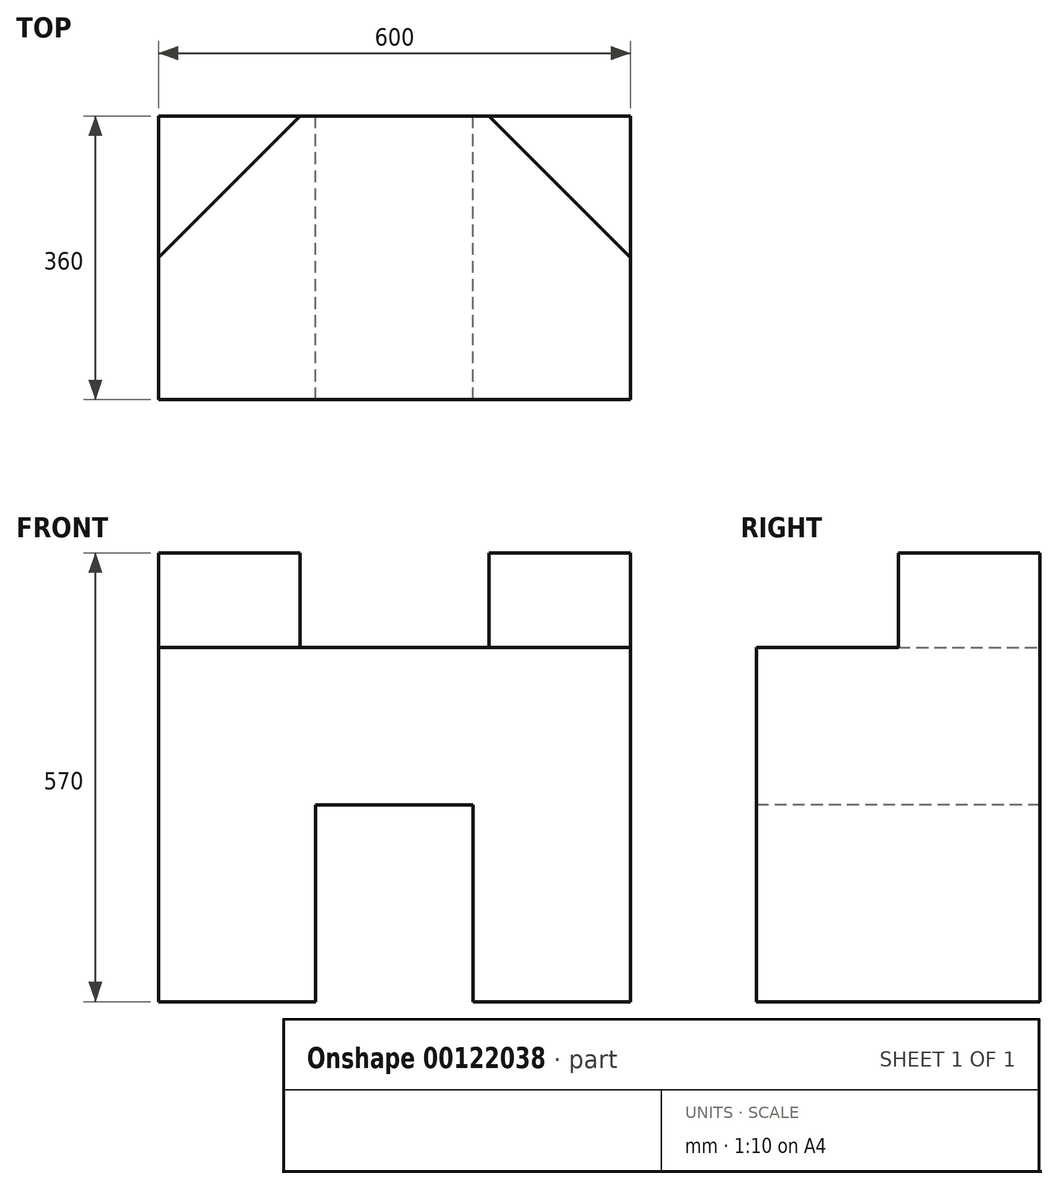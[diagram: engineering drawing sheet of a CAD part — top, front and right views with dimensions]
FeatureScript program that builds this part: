
annotation { "Feature Type Name" : "Feature", "Feature Type Description" : "" }
export const myFeature = defineFeature(function(context is Context, id is Id, definition is map)
    precondition{}
    {
        {
            var Q0;
            Q0=qCreatedBy(makeId("Front.planeOp"),FACE);
            var sketch = newSketch(context, id + "F0", { "sketchPlane" : qUnion([Q0])});
            skLineSegment(sketch, "E0.bottom", {"start": v(-300, -285) * mm, "end": v(300, -285) * mm});
            skLineSegment(sketch, "E0.top", {"start": v(-300, 285) * mm, "end": v(300, 285) * mm});
            skLineSegment(sketch, "E0.left", {"start": v(-300, -285) * mm, "end": v(-300, 285) * mm});
            skLineSegment(sketch, "E0.right", {"start": v(300, -285) * mm, "end": v(300, 285) * mm});
            skPoint(sketch, "E0.middle", {"position": v(0, 0) * mm});
            skSolve(sketch);
        }
        {
            var Q0;
            Q0 = qSketchRegion(id + "F0", true);
            extrude(context, id + "F1", {"entities" : qUnion([Q0]), "depth" : 360 * mm});
        }
        {
            var Q0;
            Q0=makeQuery(id+"F1.opExtrude","CAP_FACE",FACE,{"disambiguationData":[OSD([sQuery(id+"F0.wireOp",EDGE,"E0.bottom"),sQuery(id+"F0.wireOp",EDGE,"E0.top"),sQuery(id+"F0.wireOp",EDGE,"E0.left"),sQuery(id+"F0.wireOp",EDGE,"E0.right")])],"isStart":false});
            var sketch = newSketch(context, id + "F2", { "sketchPlane" : qUnion([Q0])});
            skLineSegment(sketch, "E1.bottom", {"start": v(-100, -535) * mm, "end": v(100, -535) * mm});
            skLineSegment(sketch, "E1.top", {"start": v(-100, -35) * mm, "end": v(100, -35) * mm});
            skLineSegment(sketch, "E1.left", {"start": v(-100, -535) * mm, "end": v(-100, -35) * mm});
            skLineSegment(sketch, "E1.right", {"start": v(100, -535) * mm, "end": v(100, -35) * mm});
            skPoint(sketch, "E1.middle", {"position": v(0, -285) * mm});
            skSolve(sketch);
        }
        {
            var Q0;
            Q0 = qSketchRegion(id + "F2", true);
            extrude(context, id + "F3", {"entities" : qUnion([Q0]), "operationType" : NewBodyOperationType.REMOVE, "endBound" : BoundingType.THROUGH_ALL, "oppositeDirection" : true, "depth" : 25 * mm});
        }
        {
            var Q0;
            Q0=makeQuery(id+"F1.opExtrude","SWEPT_FACE",FACE,{"disambiguationData":[OSD([sQuery(id+"F0.wireOp",EDGE,"E0.top")])]});
            var sketch = newSketch(context, id + "F4", { "sketchPlane" : qUnion([Q0])});
            skLineSegment(sketch, "E2", {"start": v(-300, -360) * mm, "end": v(-300, -180) * mm});
            skLineSegment(sketch, "E3", {"start": v(-300, -180) * mm, "end": v(-120, 0) * mm});
            skLineSegment(sketch, "E4", {"start": v(-120, 0) * mm, "end": v(120, 0) * mm});
            skLineSegment(sketch, "E5", {"start": v(120, 0) * mm, "end": v(300, -180) * mm});
            skLineSegment(sketch, "E6", {"start": v(300, -180) * mm, "end": v(300, -360) * mm});
            skLineSegment(sketch, "E7", {"start": v(300, -360) * mm, "end": v(-300, -360) * mm});
            skSolve(sketch);
        }
        {
            var Q0;
            Q0 = qSketchRegion(id + "F4", true);
            extrude(context, id + "F5", {"entities" : qUnion([Q0]), "operationType" : NewBodyOperationType.REMOVE, "oppositeDirection" : true, "depth" : 120 * mm});
        }
    });
